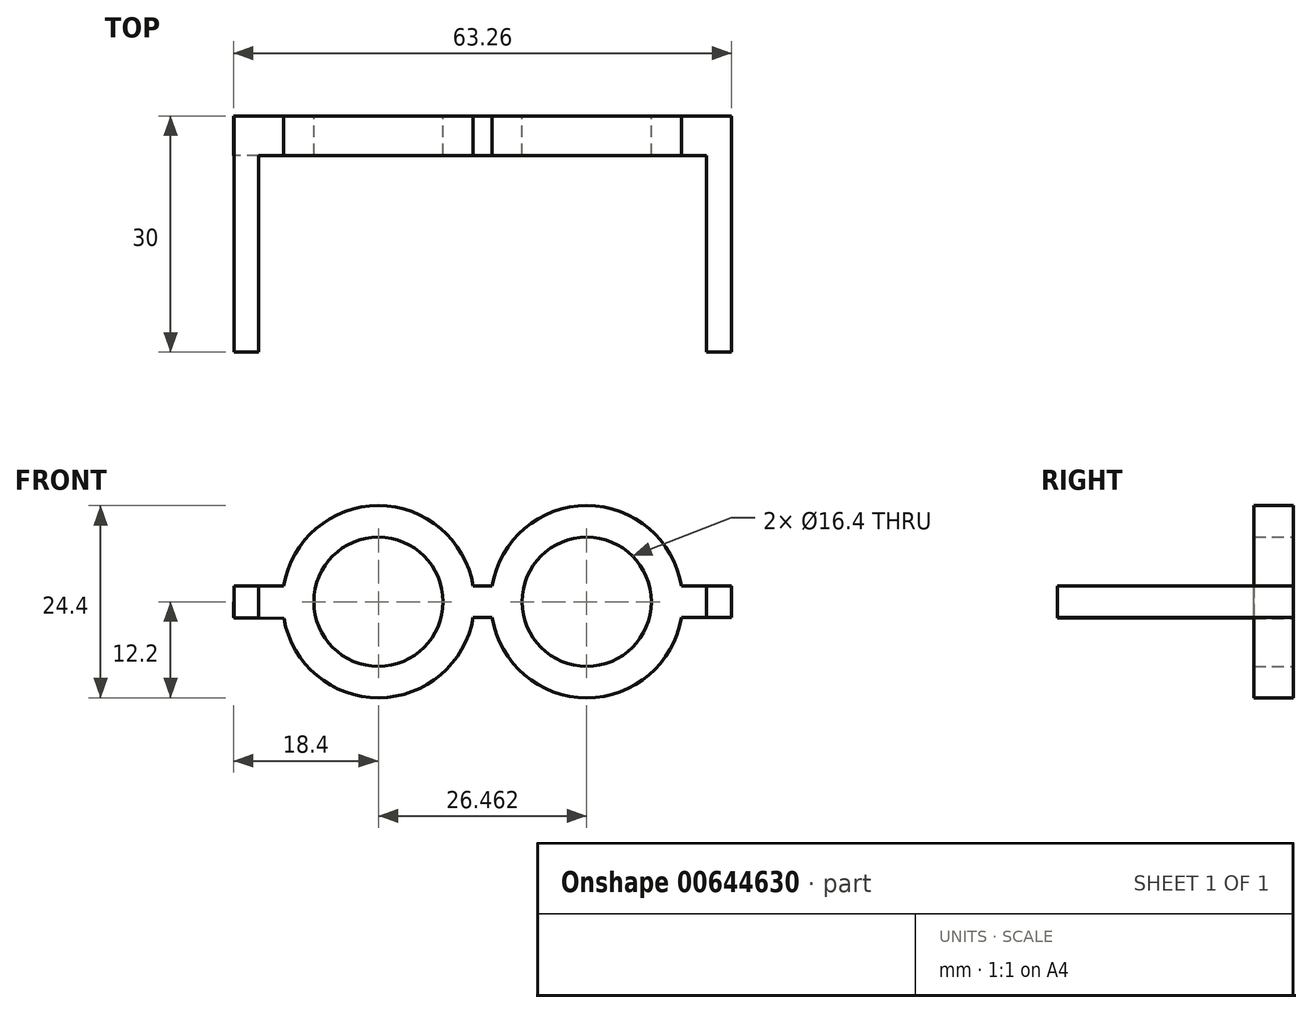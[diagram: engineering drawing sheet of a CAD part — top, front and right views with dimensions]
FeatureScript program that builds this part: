
annotation { "Feature Type Name" : "Feature", "Feature Type Description" : "" }
export const myFeature = defineFeature(function(context is Context, id is Id, definition is map)
    precondition{}
    {
        {
            var Q0;
            Q0=qCreatedBy(makeId("Front.planeOp"),FACE);
            var sketch = newSketch(context, id + "F0", { "sketchPlane" : qUnion([Q0])});
            skCircle(sketch, "E0", {"center": v(0, 0) * mm, "radius": 8.2 * mm});
            skArc(sketch, "E1.0", {"start": v(-12.01, -2.12) * mm, "mid": v(0.06, -12.2) * mm, "end": v(12.03, -2) * mm});
            skCircle(sketch, "E2", {"center": v(26.46, 0) * mm, "radius": 8.2 * mm});
            skArc(sketch, "E3.0", {"start": v(38.5, 2) * mm, "mid": v(26.46, 12.2) * mm, "end": v(14.43, 2) * mm});
            skLineSegment(sketch, "E4.bottom", {"start": v(14.43, -2) * mm, "end": v(12.03, -2) * mm});
            skLineSegment(sketch, "E4.top", {"start": v(14.43, 2) * mm, "end": v(12.03, 2) * mm});
            skPoint(sketch, "E4.middle", {"position": v(14.32, 0) * mm});
            skLineSegment(sketch, "E5.bottom", {"start": v(44.86, -2) * mm, "end": v(38.5, -2) * mm});
            skLineSegment(sketch, "E5.top", {"start": v(44.86, 2) * mm, "end": v(38.5, 2) * mm});
            skLineSegment(sketch, "E5.left", {"start": v(44.86, -2) * mm, "end": v(44.86, 2) * mm});
            skPoint(sketch, "E5.middle", {"position": v(35.66, 0) * mm});
            skLineSegment(sketch, "E6.left", {"start": v(0, -2) * mm, "end": v(0.05, 2) * mm});
            skLineSegment(sketch, "E6.right", {"start": v(-18.4, -2) * mm, "end": v(-18.35, 2) * mm});
            skPoint(sketch, "E6.middle", {"position": v(-9.17, 0) * mm});
            skPoint(sketch, "E7.orphan", {"position": v(26.46, -2) * mm});
            skPoint(sketch, "E5.right.end.orphan", {"position": v(26.46, 2) * mm});
            skLineSegment(sketch, "E8.trimOffspring", {"start": v(-12.03, 2) * mm, "end": v(-18.35, 2) * mm});
            skLineSegment(sketch, "E9.trimOffspring", {"start": v(-12.01, -2.12) * mm, "end": v(-18.4, -2) * mm});
            skArc(sketch, "E10.trimOffspring", {"start": v(14.43, -2) * mm, "mid": v(26.46, -12.2) * mm, "end": v(38.5, -2) * mm});
            skPoint(sketch, "E4.left.end.orphan", {"position": v(18.5, 2) * mm});
            skPoint(sketch, "E11.orphan", {"position": v(18.5, -2) * mm});
            skPoint(sketch, "E12.orphan", {"position": v(10.13, -2) * mm});
            skPoint(sketch, "E13.orphan", {"position": v(10.13, 2) * mm});
            skArc(sketch, "E14.trimOffspring", {"start": v(12.03, 2) * mm, "mid": v(0, 12.2) * mm, "end": v(-12.03, 2) * mm});
            skSolve(sketch);
        }
        {
            var Q0;
            Q0 = qSketchRegion(id + "F0", true);
            extrude(context, id + "F1", {"entities" : qUnion([Q0]), "depth" : 5 * mm, "offsetDistance" : 25 * mm});
        }
        {
            var Q0;
            Q0=makeQuery(id+"F1.opExtrude","CAP_FACE",FACE,{"disambiguationData":[OSD([sQuery(id+"F0.wireOp",EDGE,"E0"),sQuery(id+"F0.wireOp",EDGE,"E1.0"),sQuery(id+"F0.wireOp",EDGE,"E2"),sQuery(id+"F0.wireOp",EDGE,"E3.0"),sQuery(id+"F0.wireOp",EDGE,"E4.bottom"),sQuery(id+"F0.wireOp",EDGE,"E4.top"),sQuery(id+"F0.wireOp",EDGE,"E5.bottom"),sQuery(id+"F0.wireOp",EDGE,"E5.top"),sQuery(id+"F0.wireOp",EDGE,"E5.left"),sQuery(id+"F0.wireOp",EDGE,"E6.right"),sQuery(id+"F0.wireOp",EDGE,"E8.trimOffspring"),sQuery(id+"F0.wireOp",EDGE,"E9.trimOffspring"),sQuery(id+"F0.wireOp",EDGE,"E10.trimOffspring"),sQuery(id+"F0.wireOp",EDGE,"E14.trimOffspring")])],"isStart":false});
            var sketch = newSketch(context, id + "F2", { "sketchPlane" : qUnion([Q0])});
            skLineSegment(sketch, "E15.bottom", {"start": v(-18.35, 2) * mm, "end": v(-15.2, 2) * mm});
            skLineSegment(sketch, "E15.top", {"start": v(-18.35, -2.06) * mm, "end": v(-15.2, -2.06) * mm});
            skLineSegment(sketch, "E15.left", {"start": v(-18.35, 2) * mm, "end": v(-18.35, -2.06) * mm});
            skLineSegment(sketch, "E15.right", {"start": v(-15.2, 2) * mm, "end": v(-15.2, -2.06) * mm});
            skLineSegment(sketch, "E16.bottom", {"start": v(41.68, 2) * mm, "end": v(44.86, 2) * mm});
            skLineSegment(sketch, "E16.top", {"start": v(41.68, -2) * mm, "end": v(44.86, -2) * mm});
            skLineSegment(sketch, "E16.left", {"start": v(41.68, 2) * mm, "end": v(41.68, -2) * mm});
            skLineSegment(sketch, "E16.right", {"start": v(44.86, 2) * mm, "end": v(44.86, -2) * mm});
            skSolve(sketch);
        }
        {
            var Q0;
            Q0 = qSketchRegion(id + "F2", true);
            extrude(context, id + "F3", {"entities" : qUnion([Q0]), "operationType" : NewBodyOperationType.ADD, "depth" : 25 * mm, "offsetDistance" : 25 * mm});
        }
    });
